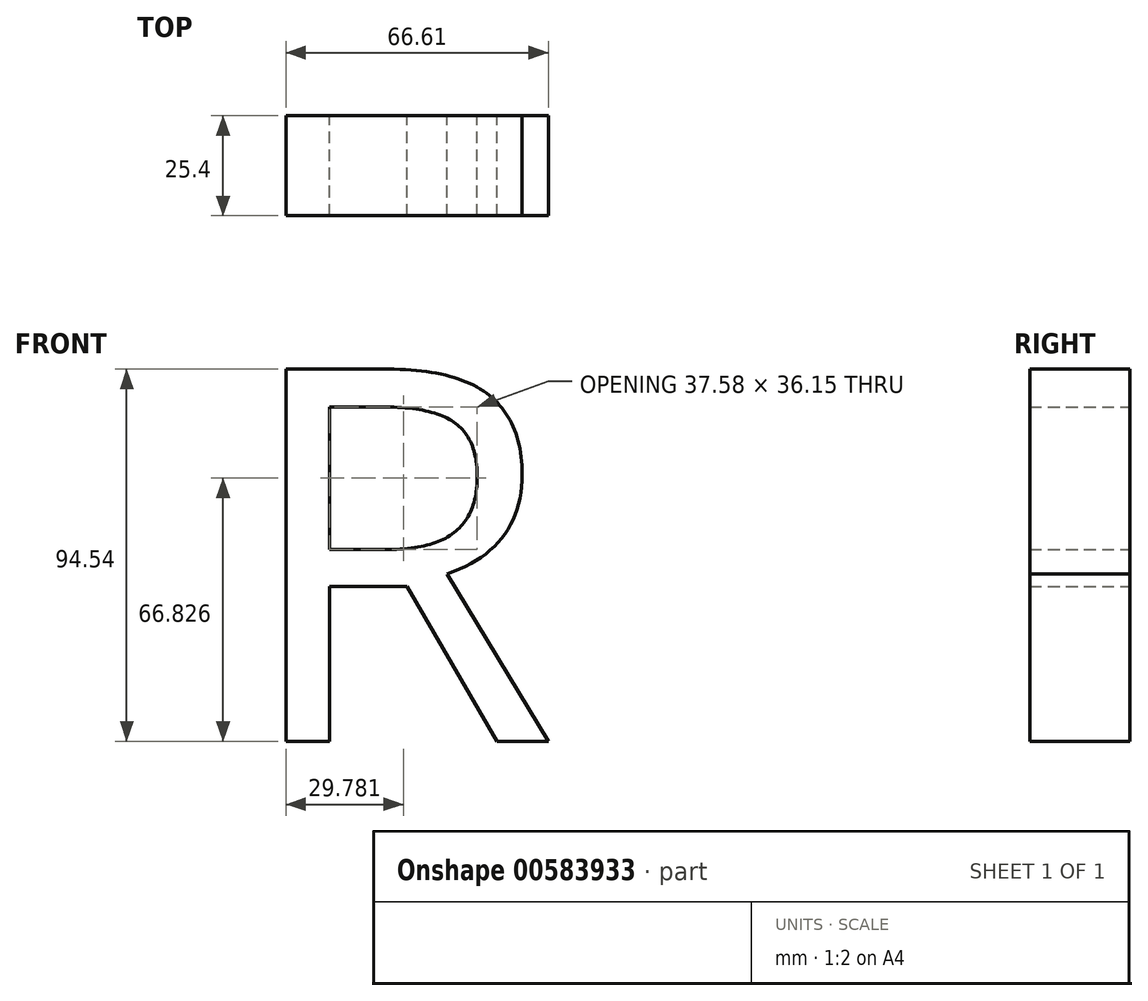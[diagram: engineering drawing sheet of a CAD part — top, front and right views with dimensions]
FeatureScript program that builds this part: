
annotation { "Feature Type Name" : "Feature", "Feature Type Description" : "" }
export const myFeature = defineFeature(function(context is Context, id is Id, definition is map)
    precondition{}
    {
        {
            var Q0;
            Q0=qCreatedBy(makeId("Front.planeOp"),FACE);
            var sketch = newSketch(context, id + "F0", { "sketchPlane" : qUnion([Q0])});
            skText(sketch, "E0", { "text": "R\n", "fontName": "OpenSans-Regular.ttf"});
            const initialGuessF0  = {"E0": [-0.0537, -0.05098, 1, 0, 0.09535]};
            skSetInitialGuess(sketch, initialGuessF0);
            skSolve(sketch);
        }
        {
            var Q0;
            Q0 = qSketchRegion(id + "F0", true);
            extrude(context, id + "F1", {"entities" : qUnion([Q0]), "depth" : 25.4 * mm, "offsetDistance" : 25.4 * mm});
        }
    });
